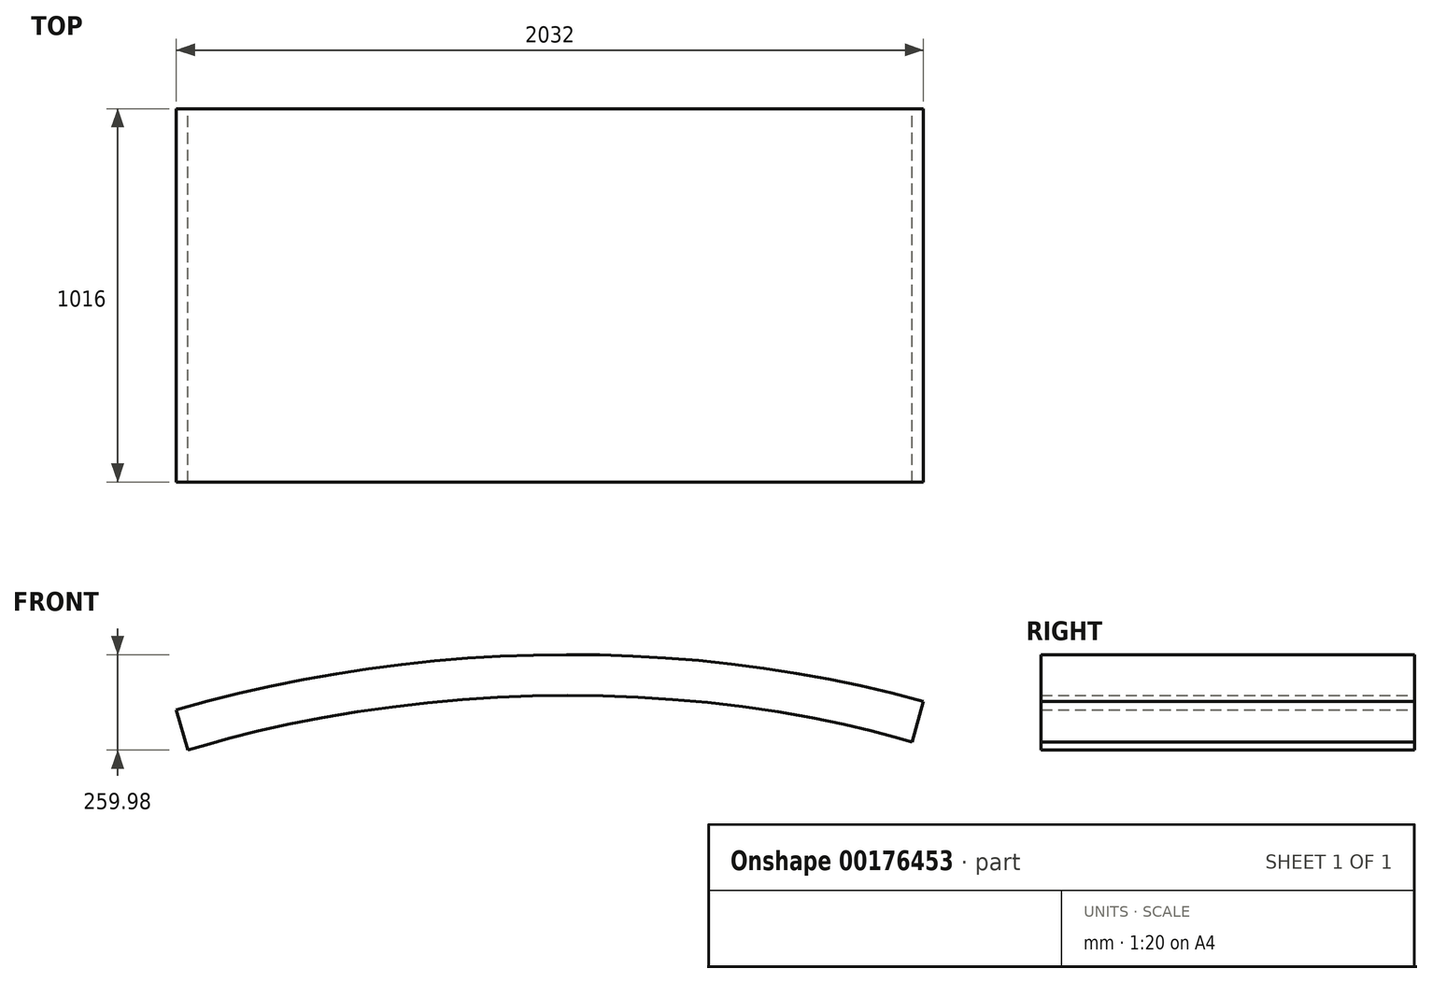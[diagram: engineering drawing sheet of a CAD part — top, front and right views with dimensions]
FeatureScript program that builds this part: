
annotation { "Feature Type Name" : "Feature", "Feature Type Description" : "" }
export const myFeature = defineFeature(function(context is Context, id is Id, definition is map)
    precondition{}
    {
        {
            var Q0;
            Q0=qCreatedBy(makeId("Front.planeOp"),FACE);
            var sketch = newSketch(context, id + "F0", { "sketchPlane" : qUnion([Q0])});
            skFitSpline(sketch, "E0", {"points": [v(-948.89, 0) * mm, v(1083.11, 22.72) * mm], "startDerivative": vector(1957.02, 564.94) * mm, "endDerivative": vector(1956.21, -542.52) * mm});
            skFitSpline(sketch, "E1.0", {"points": [v(-917.18, -109.82) * mm, v(-838.16, -87) * mm, v(-677.74, -46.6) * mm, v(-431.79, -1.94) * mm, v(-182.33, 26.45) * mm, v(68.81, 38.3) * mm, v(319.8, 33.36) * mm, v(568.84, 11.38) * mm, v(814.1, -27.84) * mm, v(973.9, -65.6) * mm, v(1052.57, -87.42) * mm]});
            skLineSegment(sketch, "E2", {"start": v(-948.89, 0) * mm, "end": v(-917.18, -109.82) * mm});
            skLineSegment(sketch, "E3", {"start": v(1083.11, 22.72) * mm, "end": v(1052.57, -87.42) * mm});
            skSolve(sketch);
        }
        {
            var Q0;
            Q0 = qSketchRegion(id + "F0", true);
            extrude(context, id + "F1", {"entities" : qUnion([Q0]), "depth" : 1016 * mm});
        }
    });
